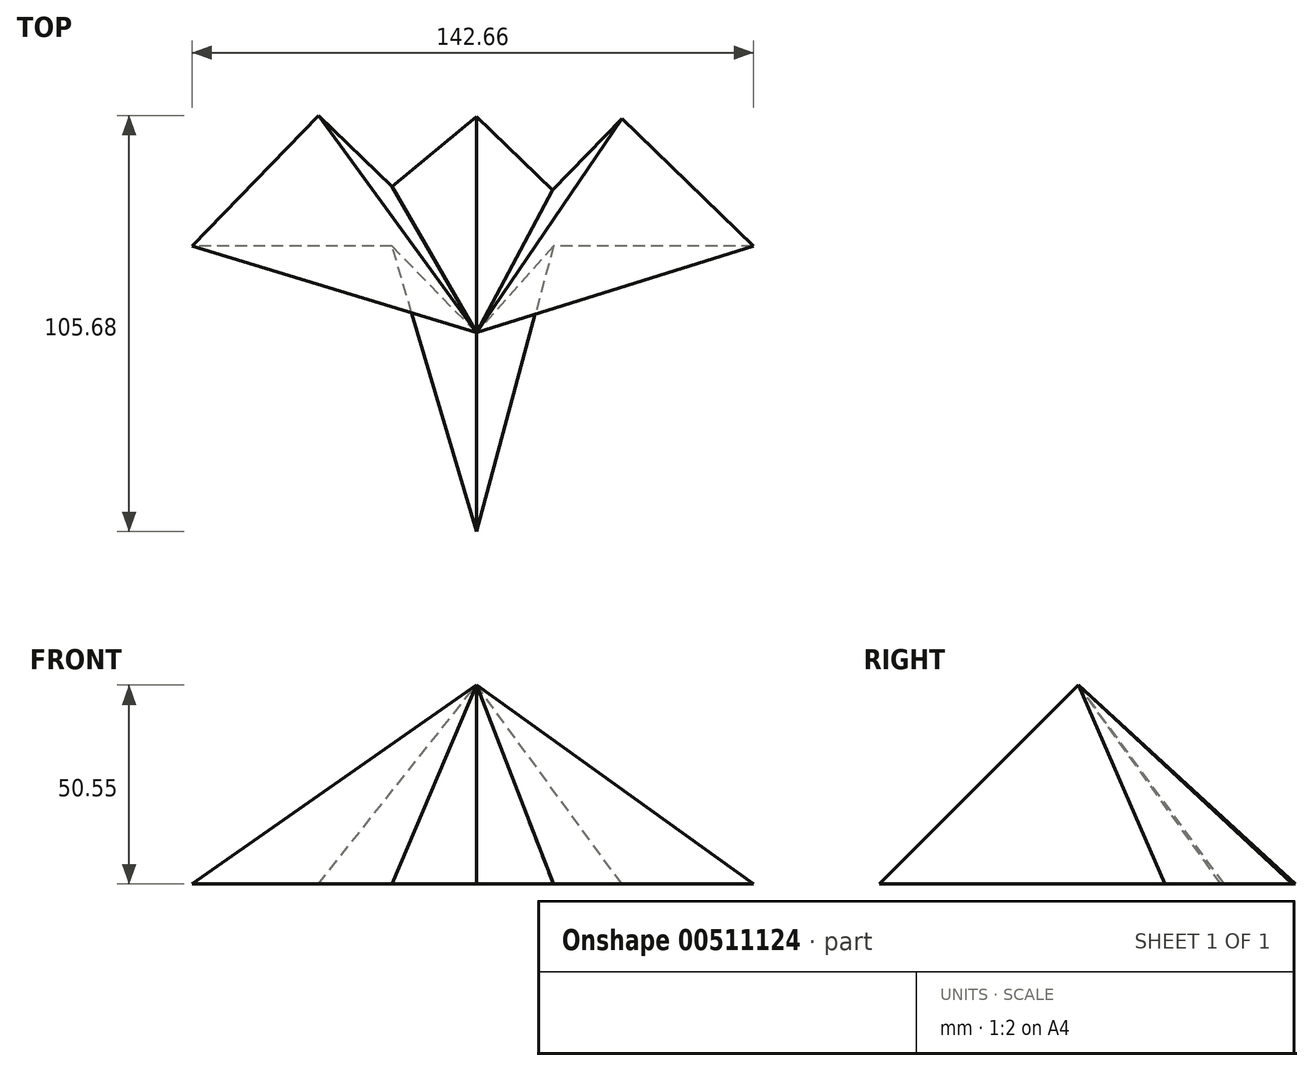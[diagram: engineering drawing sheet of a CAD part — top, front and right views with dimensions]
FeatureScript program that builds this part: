
annotation { "Feature Type Name" : "Feature", "Feature Type Description" : "" }
export const myFeature = defineFeature(function(context is Context, id is Id, definition is map)
    precondition{}
    {
        {
            var Q0;
            Q0=qCreatedBy(makeId("Top.planeOp"),FACE);
            var sketch = newSketch(context, id + "F0", { "sketchPlane" : qUnion([Q0])});
            skLineSegment(sketch, "E0", {"start": v(0, 46.73) * mm, "end": v(19.3, 28.04) * mm});
            skLineSegment(sketch, "E1", {"start": v(19.3, 28.04) * mm, "end": v(36.94, 46.25) * mm});
            skLineSegment(sketch, "E2", {"start": v(36.94, 46.25) * mm, "end": v(70.4, 13.85) * mm});
            skLineSegment(sketch, "E3", {"start": v(70.4, 13.85) * mm, "end": v(19.6, 13.85) * mm});
            skLineSegment(sketch, "E4", {"start": v(19.6, 13.85) * mm, "end": v(0, -58.68) * mm});
            skLineSegment(sketch, "E5", {"start": v(0, -58.68) * mm, "end": v(-21.45, 13.85) * mm});
            skLineSegment(sketch, "E6", {"start": v(-21.45, 13.85) * mm, "end": v(-72.25, 13.85) * mm});
            skLineSegment(sketch, "E7", {"start": v(-72.25, 13.85) * mm, "end": v(-40.15, 47) * mm});
            skLineSegment(sketch, "E8", {"start": v(-40.15, 47) * mm, "end": v(-21.45, 28.9) * mm});
            skLineSegment(sketch, "E9", {"start": v(-21.45, 28.9) * mm, "end": v(0, 46.73) * mm});
            skSolve(sketch);
        }
        {
            var Q0;
            Q0=qCreatedBy(makeId("Top.planeOp"),FACE);
            cPlane(context, id + "F1", {"entities" : qUnion([Q0]), "cplaneType" : CPlaneType.OFFSET, "offset" : 50.55 * mm, "width" : 152.4 * mm, "height" : 152.4 * mm});
        }
        {
            var Q0;
            Q0=qCreatedBy(id+"F1.planeOp",FACE);
            var sketch = newSketch(context, id + "F2", { "sketchPlane" : qUnion([Q0])});
            skPoint(sketch, "E10", {"position": v(0, -8.14) * mm});
            skSolve(sketch);
        }
        {
            var Q0;
            Q0=makeQuery(id+"F0.imprint","IMPRINT",FACE,{"disambiguationData":[TD([[makeQuery(id+"F0.imprint","IMPRINT",EDGE,{"derivedFrom":sQuery(id+"F0.wireOp",EDGE,"E0")}),-1.0]])]});
            var Q1;
            Q1=sQuery(id+"F2.wireOp",VERTEX,"E10");
            loft(context, id + "F3", {"sheetProfilesArray" : [{ "sheetProfileEntities" : qUnion([Q0]) }, { "sheetProfileEntities" : qUnion([Q1]) }]});
        }
    });
